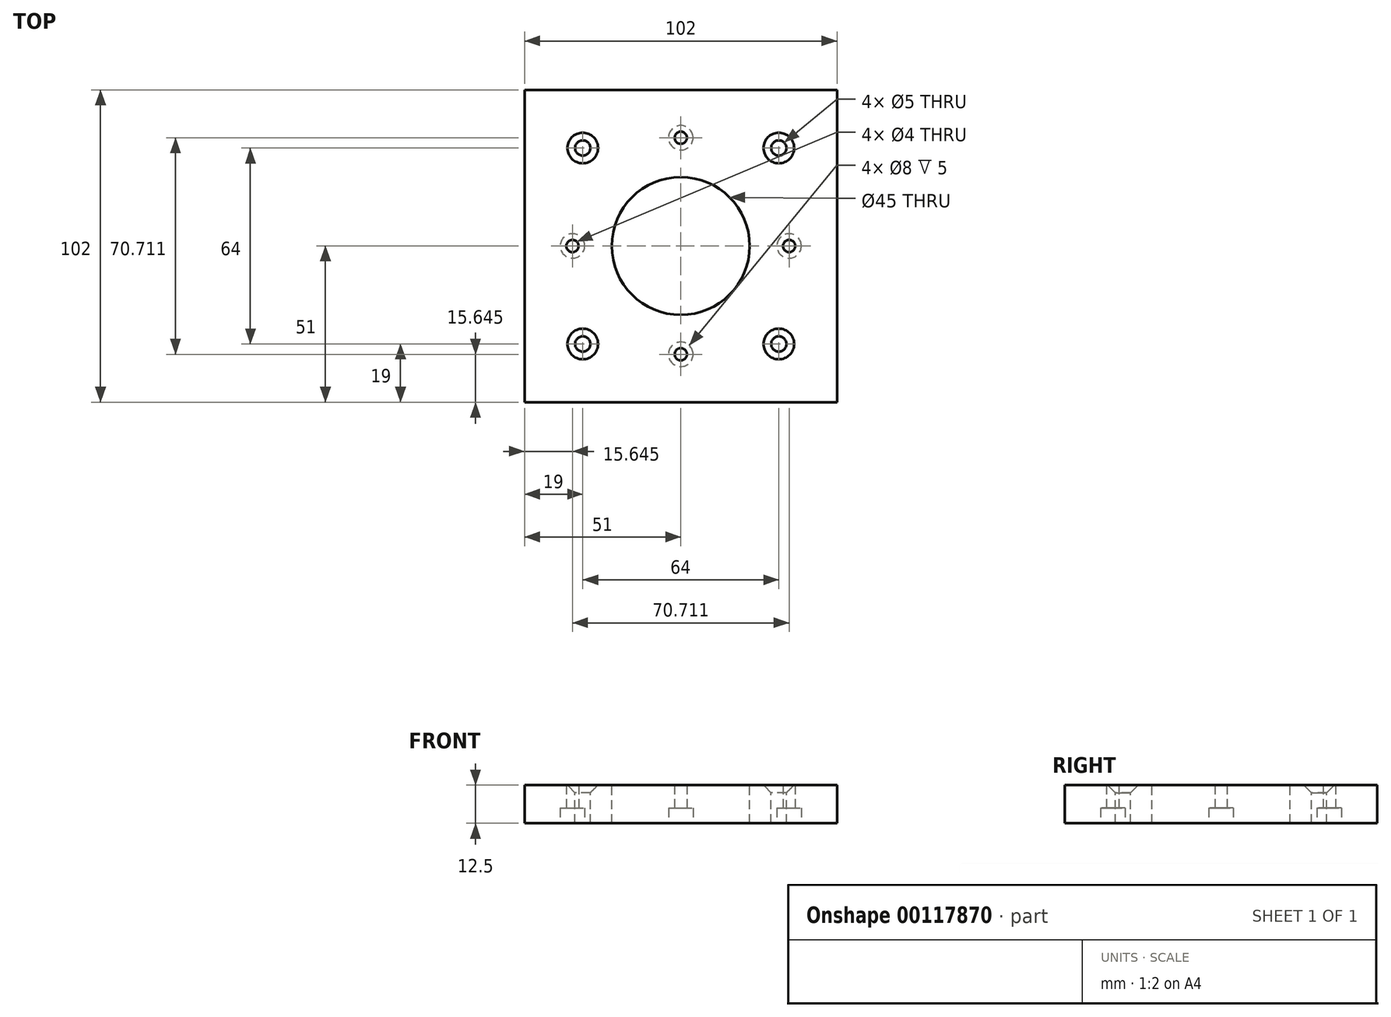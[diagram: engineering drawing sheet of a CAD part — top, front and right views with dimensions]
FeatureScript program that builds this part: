
annotation { "Feature Type Name" : "Feature", "Feature Type Description" : "" }
export const myFeature = defineFeature(function(context is Context, id is Id, definition is map)
    precondition{}
    {
        {
            var Q0;
            Q0=qCreatedBy(makeId("Top.planeOp"),FACE);
            var sketch = newSketch(context, id + "F3", { "sketchPlane" : qUnion([Q0])});
            skLineSegment(sketch, "E0.bottom", {"start": v(0, 0) * mm, "end": v(102, 0) * mm});
            skLineSegment(sketch, "E0.top", {"start": v(0, 102) * mm, "end": v(102, 102) * mm});
            skLineSegment(sketch, "E0.left", {"start": v(0, 0) * mm, "end": v(0, 102) * mm});
            skLineSegment(sketch, "E0.right", {"start": v(102, 0) * mm, "end": v(102, 102) * mm});
            skSolve(sketch);
        }
        {
            var Q0;
            Q0=makeQuery(id+"F3.imprint","IMPRINT",FACE,{"disambiguationData":[TD([[makeQuery(id+"F3.imprint","IMPRINT",EDGE,{"derivedFrom":sQuery(id+"F3.wireOp",EDGE,"E0.bottom")}),1.0]])]});
            extrude(context, id + "F4", {"entities" : qUnion([Q0]), "depth" : 12.5 * mm});
        }
        {
            var Q0;
            Q0=makeQuery(id+"F4.opExtrude","CAP_FACE",FACE,{"disambiguationData":[OSD([sQuery(id+"F3.wireOp",EDGE,"E0.bottom"),sQuery(id+"F3.wireOp",EDGE,"E0.top"),sQuery(id+"F3.wireOp",EDGE,"E0.left"),sQuery(id+"F3.wireOp",EDGE,"E0.right")])],"isStart":false});
            var sketch = newSketch(context, id + "F0", { "sketchPlane" : qUnion([Q0])});
            skPoint(sketch, "E1", {"position": v(51, 51) * mm});
            skSolve(sketch);
        }
        {
            var Q0;
            Q0=sQuery(id+"F0.wireOp",VERTEX,"E1");
            var Q1;
            Q1=makeQuery(id+"F4.opExtrude","SWEPT_BODY",BODY,{"disambiguationData":[OSD([sQuery(id+"F3.wireOp",EDGE,"E0.bottom"),sQuery(id+"F3.wireOp",EDGE,"E0.top"),sQuery(id+"F3.wireOp",EDGE,"E0.left"),sQuery(id+"F3.wireOp",EDGE,"E0.right")])]});
            hole(context, id + "F5", {"style" : HoleStyle.SIMPLE, "endStyle" : HoleEndStyle.THROUGH, "holeDiameter" : 45 * mm, "locations" : qUnion([Q0]), "scope" : qUnion([Q1]), "isTappedThrough" : true});
        }
        {
            var Q0;
            Q0=makeQuery(id+"F4.opExtrude","CAP_FACE",FACE,{"disambiguationData":[OSD([sQuery(id+"F3.wireOp",EDGE,"E0.bottom"),sQuery(id+"F3.wireOp",EDGE,"E0.top"),sQuery(id+"F3.wireOp",EDGE,"E0.left"),sQuery(id+"F3.wireOp",EDGE,"E0.right")])],"isStart":false});
            var sketch = newSketch(context, id + "F6", { "sketchPlane" : qUnion([Q0])});
            skPoint(sketch, "E2", {"position": v(19, 19) * mm});
            skPoint(sketch, "E3", {"position": v(83, 19) * mm});
            skPoint(sketch, "E4", {"position": v(83, 83) * mm});
            skPoint(sketch, "E5", {"position": v(19, 83) * mm});
            skSolve(sketch);
        }
        {
            var Q0;
            Q0=sQuery(id+"F6.wireOp",VERTEX,"E2");
            var Q1;
            Q1=makeQuery(id+"F4.opExtrude","SWEPT_BODY",BODY,{"disambiguationData":[OSD([sQuery(id+"F3.wireOp",EDGE,"E0.bottom"),sQuery(id+"F3.wireOp",EDGE,"E0.top"),sQuery(id+"F3.wireOp",EDGE,"E0.left"),sQuery(id+"F3.wireOp",EDGE,"E0.right")])]});
            hole(context, id + "F1", {"style" : HoleStyle.C_SINK, "endStyle" : HoleEndStyle.THROUGH, "holeDiameter" : 5 * mm, "cSinkDiameter" : 10 * mm, "cSinkAngle" : 90 * degree, "locations" : qUnion([Q0]), "scope" : qUnion([Q1]), "isTappedThrough" : true});
        }
        {
            var Q0;
            Q0=sQuery(id+"F6.wireOp",VERTEX,"E4");
            var Q1;
            Q1=sQuery(id+"F6.wireOp",VERTEX,"E5");
            var Q2;
            Q2=sQuery(id+"F6.wireOp",VERTEX,"E3");
            var Q3;
            Q3=makeQuery(id+"F4.opExtrude","SWEPT_BODY",BODY,{"disambiguationData":[OSD([sQuery(id+"F3.wireOp",EDGE,"E0.bottom"),sQuery(id+"F3.wireOp",EDGE,"E0.top"),sQuery(id+"F3.wireOp",EDGE,"E0.left"),sQuery(id+"F3.wireOp",EDGE,"E0.right")])]});
            hole(context, id + "F2", {"style" : HoleStyle.C_SINK, "endStyle" : HoleEndStyle.THROUGH, "holeDiameter" : 5 * mm, "cSinkDiameter" : 10 * mm, "cSinkAngle" : 90 * degree, "locations" : qUnion([Q0, Q1, Q2]), "scope" : qUnion([Q3]), "isTappedThrough" : true});
        }
        {
            var Q0;
            Q0=makeQuery(id+"F4.opExtrude","CAP_FACE",FACE,{"disambiguationData":[OSD([sQuery(id+"F3.wireOp",EDGE,"E0.bottom"),sQuery(id+"F3.wireOp",EDGE,"E0.top"),sQuery(id+"F3.wireOp",EDGE,"E0.left"),sQuery(id+"F3.wireOp",EDGE,"E0.right")])],"isStart":true});
            var sketch = newSketch(context, id + "F7", { "sketchPlane" : qUnion([Q0])});
            skPoint(sketch, "E6", {"position": v(86.36, -51) * mm});
            skPoint(sketch, "E7", {"position": v(51, -15.64) * mm});
            skPoint(sketch, "E8", {"position": v(15.64, -51) * mm});
            skPoint(sketch, "E9", {"position": v(51, -86.36) * mm});
            skLineSegment(sketch, "E10", {"start": v(51, -51) * mm, "end": v(51, -86.36) * mm});
            skSolve(sketch);
        }
        {
            var Q0;
            Q0=sQuery(id+"F7.wireOp",VERTEX,"E8");
            var Q1;
            Q1=sQuery(id+"F7.wireOp",VERTEX,"E7");
            var Q2;
            Q2=sQuery(id+"F7.wireOp",VERTEX,"E6");
            var Q3;
            Q3=sQuery(id+"F7.wireOp",VERTEX,"E9");
            var Q4;
            Q4=makeQuery(id+"F4.opExtrude","SWEPT_BODY",BODY,{"disambiguationData":[OSD([sQuery(id+"F3.wireOp",EDGE,"E0.bottom"),sQuery(id+"F3.wireOp",EDGE,"E0.top"),sQuery(id+"F3.wireOp",EDGE,"E0.left"),sQuery(id+"F3.wireOp",EDGE,"E0.right")])]});
            hole(context, id + "F8", {"style" : HoleStyle.C_BORE, "endStyle" : HoleEndStyle.THROUGH, "holeDiameter" : 4 * mm, "cBoreDiameter" : 8 * mm, "cBoreDepth" : 5 * mm, "locations" : qUnion([Q0, Q1, Q2, Q3]), "scope" : qUnion([Q4]), "isTappedThrough" : true});
        }
    });
